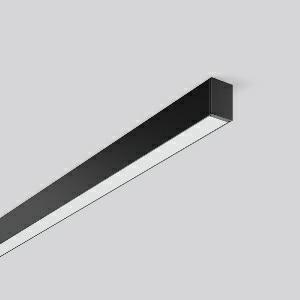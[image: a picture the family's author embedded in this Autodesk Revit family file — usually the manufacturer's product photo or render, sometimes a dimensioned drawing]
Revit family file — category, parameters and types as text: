
# Revit family: less_is_more_27_312200_003_1_9b21
name_source: partatom
category: Lighting Fixtures
units: mm (PartAtom-declared; Revit-internal decimal feet)

## family parameters
Cut with Voids When Loaded = No
Host = Face
Light Source = No
Part Type = Normal
Room Calculation Point = No
Round Connector Dimension = Use Diameter
Shared = No

## types (1)
- LESS IS MORE 27 (1 x LED Modul 840, 2400 lm, 4000)
    Apparent Load = 39 VA
    CIE Flux Codes = 48 79 96 100 100
    Color Rendering = 80
    Color Temperature = 4000
    Default Elevation = 1800 mm
    Description = Series: LESS IS MORE 27
Ceiling and wall luminaire with slim design. Housing: extruded aluminium profile, powder-coated. End cap aluminium powder-coated. Diffuser made of non-yellowing plastic (PMMA), opal. Suitable for Ceiling mounting, Wall (surface). External driver with connecting cable. 
Colour: deep black, matt (RAL 9005)
Length: 1512 mm
Width: 28 mm
Height: 38 mm
Lamp: LED
Socket: without socket
Colour temperature: 4000K
Colour rendering index (CRI): 82
System power: 39 W
Rated luminous flux: 2400 lm
Luminous efficiency: 62 lm/W
Control gear: Regulated power supply
Protection class: II
Type of protection: IP 20
    Height = 38 mm
    Lamp = 1 x LED Modul 840
    Lamp Light Flux = 2400 lm
    Lamp count = 1
    Length = 1512 mm
    Lifetime = 50000 h
    Luminous efficacy = 62 lm/W
    Manufacturer = RZB
    ModVariant = No
    Model = 312200.003.1
    Mounting Place = Wall, Ceiling
    Mounting Type = Surface mounted
    Number of Poles = 1
    OnlyDefault = Yes
    Power Factor = 1
    Product Name = LESS IS MORE 27
    Product group = Surface mounted LED linear luminaires
    ProductGroupID = 307
    Protection Class = Protection class II
    Protection Degree = IP 20
    RLX_Detail_Level = 1
    RLX_Emergency_Light_Flux = 0 lm
    RLX_Emergency_Type = 0
    RLX_Emergency_Type_DB = No
    RlxData = <blob elided: 28681 chars, md5=4b60108a>
    Socket = socket
    Standby Power = 0 W
    System Light Flux = 2400 lm
    System Power = 39 W
    Type Comments = Product without accessories
    Type Image = 312196.003.jpg
    URL = http://relux.com
    VarID = ---
    Voltage = 230 V
    Voltage Range = 220-240 V
    Weight = 0.00 kg
    Width = 28 mm

## geometry (parser evidence)
native form markers: Blend x4, Sweep x12
no freeform markers — native parametric forms only
